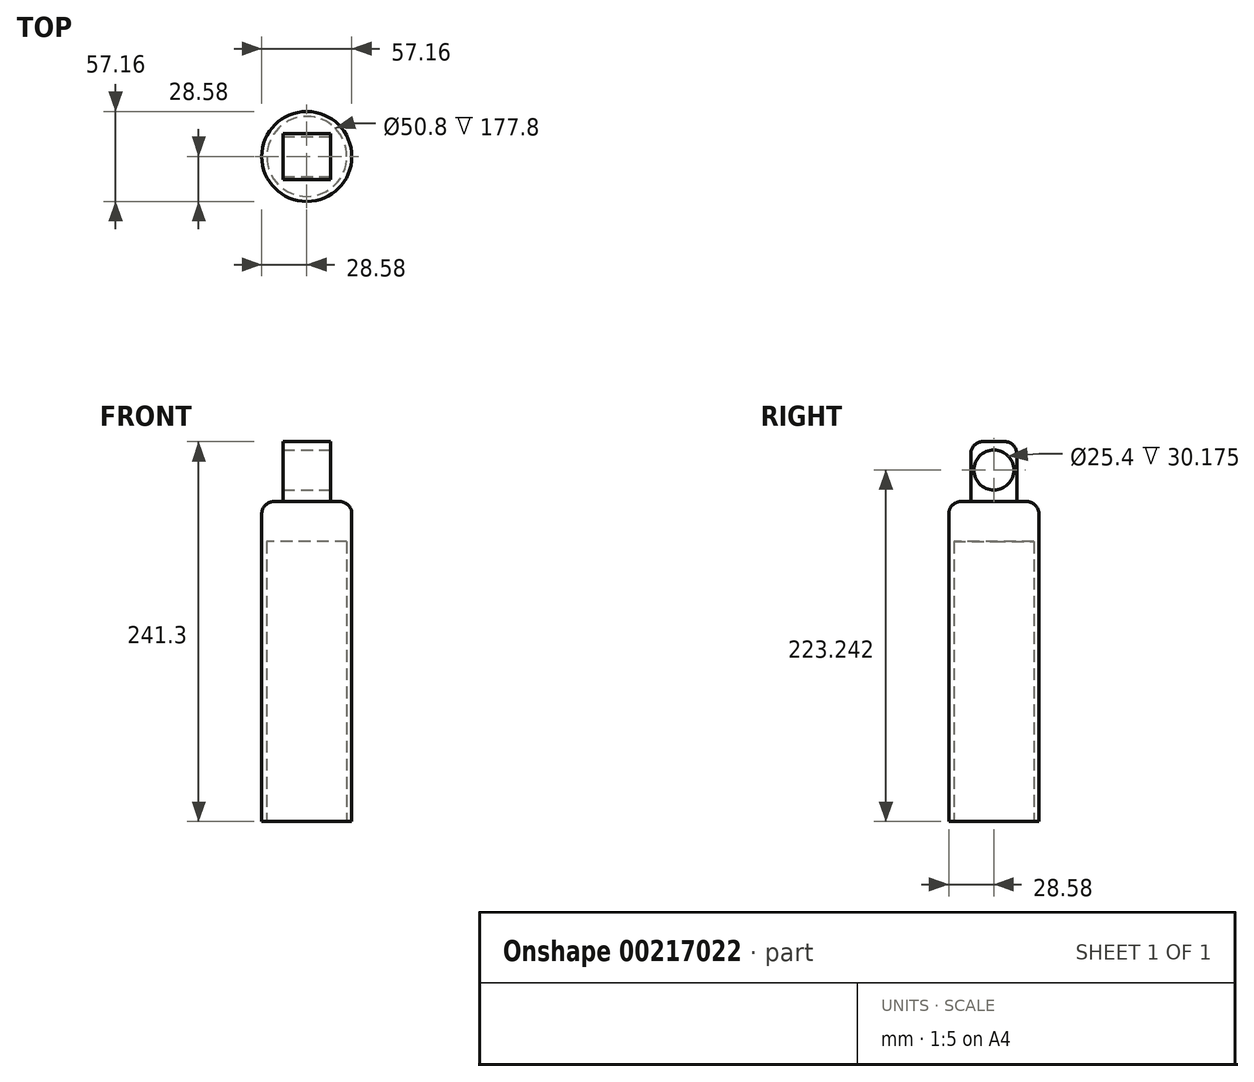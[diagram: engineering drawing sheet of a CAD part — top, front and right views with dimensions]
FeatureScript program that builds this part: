
annotation { "Feature Type Name" : "Feature", "Feature Type Description" : "" }
export const myFeature = defineFeature(function(context is Context, id is Id, definition is map)
    precondition{}
    {
        {
            var Q0;
            Q0=qCreatedBy(makeId("Top.planeOp"),FACE);
            var sketch = newSketch(context, id + "F0", { "sketchPlane" : qUnion([Q0])});
            skCircle(sketch, "E0", {"center": v(0, 0) * mm, "radius": 25.4 * mm});
            skCircle(sketch, "E1", {"center": v(0, 0) * mm, "radius": 28.58 * mm});
            skSolve(sketch);
        }
        {
            var Q0;
            Q0 = qSketchRegion(id + "F0", true);
            var Q1;
            Q1=makeQuery(id+"F0.imprint","IMPRINT",FACE,{"disambiguationData":[TD([[makeQuery(id+"F0.imprint","IMPRINT",EDGE,{"derivedFrom":sQuery(id+"F0.wireOp",EDGE,"E0")}),1.0]])]});
            extrude(context, id + "F1", {"entities" : qUnion([Q0, Q1]), "depth" : 203.2 * mm});
        }
        {
            var Q0;
            Q0=makeQuery(id+"F0.imprint","IMPRINT",FACE,{"disambiguationData":[TD([[makeQuery(id+"F0.imprint","IMPRINT",EDGE,{"derivedFrom":sQuery(id+"F0.wireOp",EDGE,"E0")}),1.0]])]});
            extrude(context, id + "F2", {"entities" : qUnion([Q0]), "operationType" : NewBodyOperationType.REMOVE, "depth" : 177.8 * mm});
        }
        {
            var Q0;
            Q0=makeQuery(id+"F1.opExtrude","CAP_EDGE",EDGE,{"disambiguationData":[OSD([sQuery(id+"F0.wireOp",EDGE,"E1")])],"isStart":false});
            fillet(context, id + "F3", {"entities" : qUnion([Q0]), "radius" : 7.62 * mm, "tangentPropagation" : true, "allowEdgeOverflow" : false});
        }
        {
            var Q0;
            Q0=makeQuery(id+"F1.opExtrude","CAP_FACE",FACE,{"disambiguationData":[OSD([sQuery(id+"F0.wireOp",EDGE,"E1")])],"isStart":false});
            var sketch = newSketch(context, id + "F4", { "sketchPlane" : qUnion([Q0])});
            skLineSegment(sketch, "E2.bottom", {"start": v(15.09, -14.54) * mm, "end": v(-15.09, -14.54) * mm});
            skLineSegment(sketch, "E2.top", {"start": v(15.09, 14.54) * mm, "end": v(-15.09, 14.54) * mm});
            skLineSegment(sketch, "E2.left", {"start": v(15.09, -14.54) * mm, "end": v(15.09, 14.54) * mm});
            skLineSegment(sketch, "E2.right", {"start": v(-15.09, -14.54) * mm, "end": v(-15.09, 14.54) * mm});
            skPoint(sketch, "E2.middle", {"position": v(0, 0) * mm});
            skSolve(sketch);
        }
        {
            var Q0;
            Q0=makeQuery(id+"F4.imprint","IMPRINT",FACE,{"disambiguationData":[TD([[makeQuery(id+"F4.imprint","IMPRINT",EDGE,{"derivedFrom":sQuery(id+"F4.wireOp",EDGE,"E2.bottom")}),-1.0]])]});
            extrude(context, id + "F5", {"entities" : qUnion([Q0]), "operationType" : NewBodyOperationType.ADD, "depth" : 38.1 * mm});
        }
        {
            var Q0;
            Q0=makeQuery(id+"F5.opExtrude","SWEPT_FACE",FACE,{"disambiguationData":[OSD([sQuery(id+"F4.wireOp",EDGE,"E2.left")])]});
            var sketch = newSketch(context, id + "F6", { "sketchPlane" : qUnion([Q0])});
            skCircle(sketch, "E3", {"center": v(0, 223.24) * mm, "radius": 12.7 * mm});
            skSolve(sketch);
        }
        {
            var Q0;
            Q0=makeQuery(id+"F5.opExtrude","CAP_EDGE",EDGE,{"disambiguationData":[OSD([sQuery(id+"F4.wireOp",EDGE,"E2.bottom")])],"isStart":false});
            var Q1;
            Q1=makeQuery(id+"F5.opExtrude","CAP_EDGE",EDGE,{"disambiguationData":[OSD([sQuery(id+"F4.wireOp",EDGE,"E2.top")])],"isStart":false});
            fillet(context, id + "F7", {"entities" : qUnion([Q0, Q1]), "radius" : 7.62 * mm, "tangentPropagation" : true, "allowEdgeOverflow" : false});
        }
        {
            var Q0;
            Q0=makeQuery(id+"F6.imprint","IMPRINT",FACE,{"disambiguationData":[TD([[makeQuery(id+"F6.imprint","IMPRINT",EDGE,{"derivedFrom":sQuery(id+"F6.wireOp",EDGE,"E3")}),1.0]])]});
            extrude(context, id + "F8", {"entities" : qUnion([Q0]), "operationType" : NewBodyOperationType.REMOVE, "endBound" : BoundingType.THROUGH_ALL, "oppositeDirection" : true, "depth" : 25.4 * mm});
        }
    });
